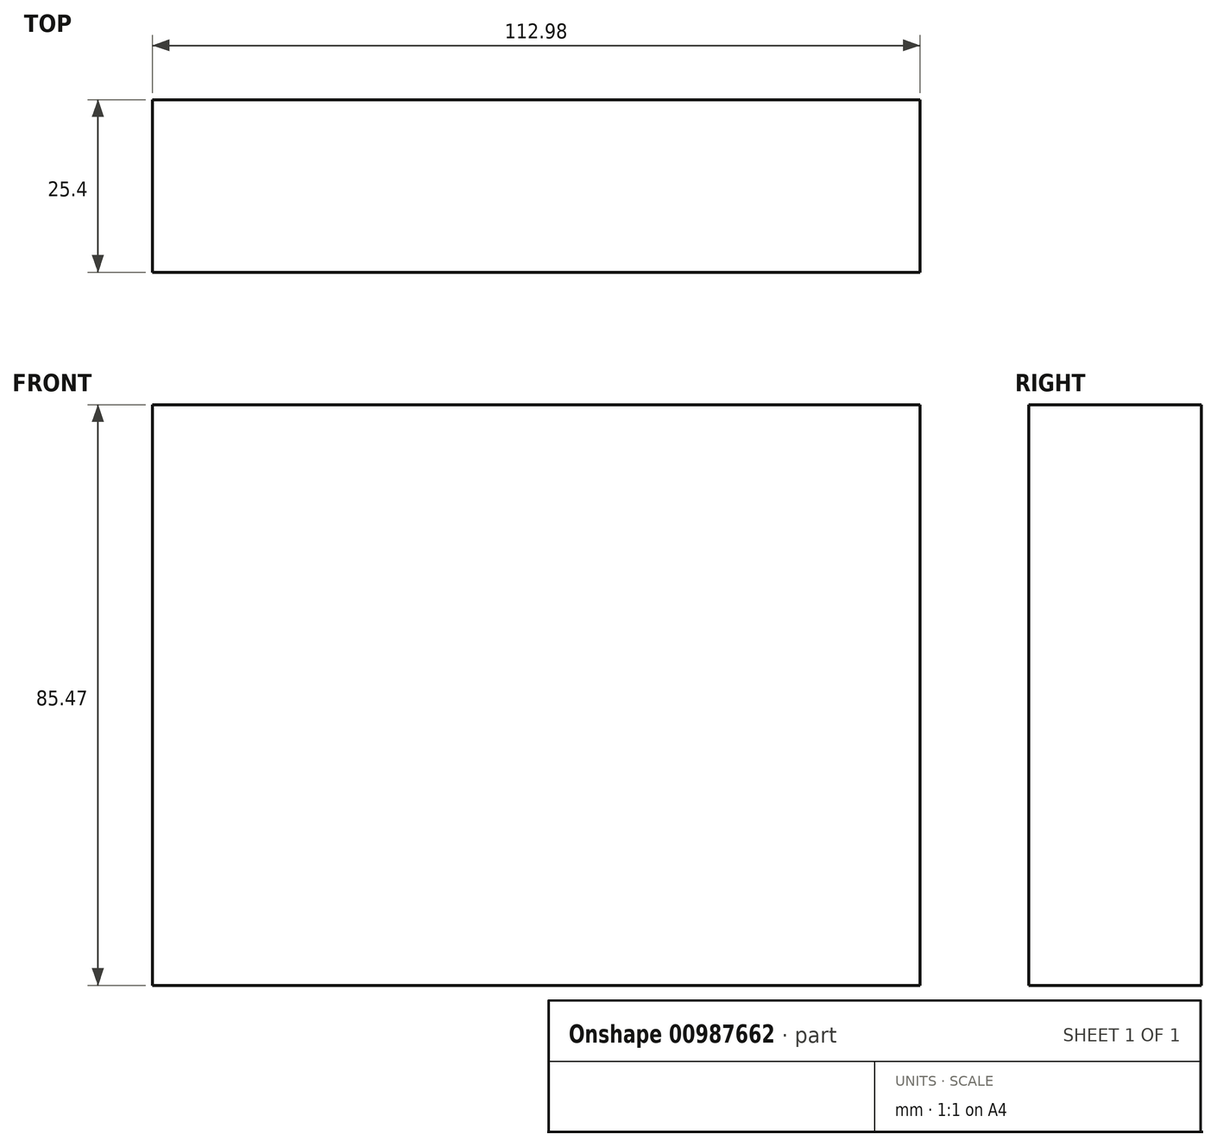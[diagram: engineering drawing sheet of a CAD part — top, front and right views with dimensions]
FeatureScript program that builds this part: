
annotation { "Feature Type Name" : "Feature", "Feature Type Description" : "" }
export const myFeature = defineFeature(function(context is Context, id is Id, definition is map)
    precondition{}
    {
        {
            var Q0;
            Q0=qCreatedBy(makeId("Front.planeOp"),FACE);
            var sketch = newSketch(context, id + "F0", { "sketchPlane" : qUnion([Q0])});
            skLineSegment(sketch, "E0.bottom", {"start": v(-137.64, 66.19) * mm, "end": v(-24.66, 66.19) * mm});
            skLineSegment(sketch, "E0.top", {"start": v(-137.64, -19.28) * mm, "end": v(-24.66, -19.28) * mm});
            skLineSegment(sketch, "E0.left", {"start": v(-137.64, 66.19) * mm, "end": v(-137.64, -19.28) * mm});
            skLineSegment(sketch, "E0.right", {"start": v(-24.66, 66.19) * mm, "end": v(-24.66, -19.28) * mm});
            skCircle(sketch, "E1", {"center": v(172.34, 21.52) * mm, "radius": 63.5 * mm});
            skSolve(sketch);
        }
        {
            var Q0;
            Q0=makeQuery(id+"F0.imprint","IMPRINT",FACE,{"disambiguationData":[TD([[makeQuery(id+"F0.imprint","IMPRINT",EDGE,{"derivedFrom":sQuery(id+"F0.wireOp",EDGE,"E0.bottom")}),-1.0]])]});
            extrude(context, id + "F1", {"entities" : qUnion([Q0]), "depth" : 25.4 * mm, "offsetDistance" : 25.4 * mm});
        }
    });
